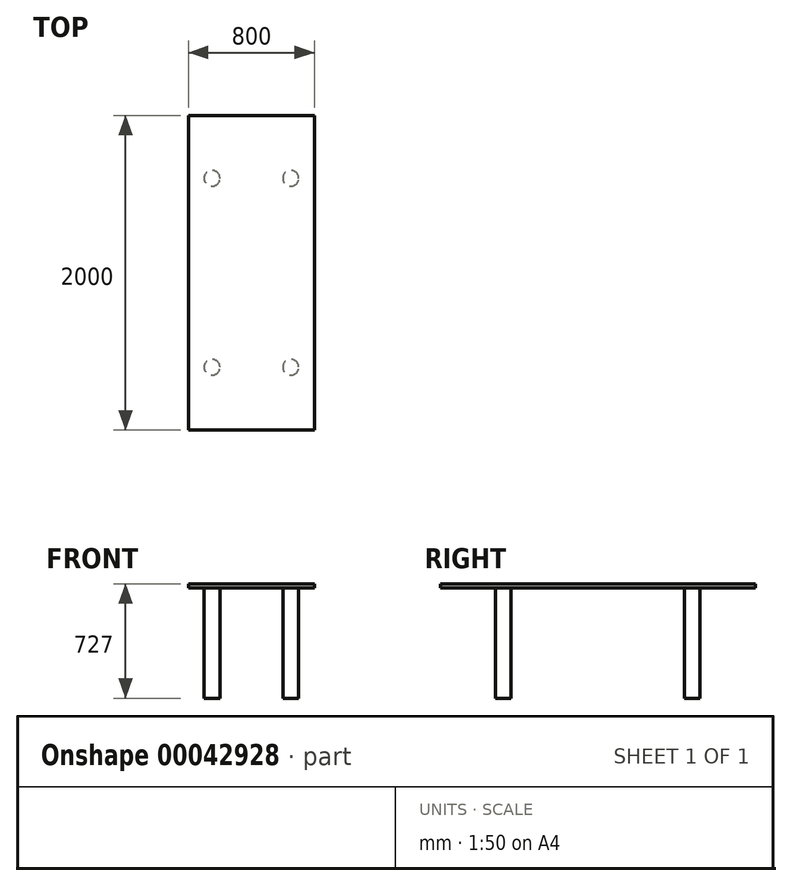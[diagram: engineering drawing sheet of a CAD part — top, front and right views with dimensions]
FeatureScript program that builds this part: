
annotation { "Feature Type Name" : "Feature", "Feature Type Description" : "" }
export const myFeature = defineFeature(function(context is Context, id is Id, definition is map)
    precondition{}
    {
        {
            var Q0;
            Q0=qCreatedBy(makeId("Front.planeOp"),FACE);
            var sketch = newSketch(context, id + "F0", { "sketchPlane" : qUnion([Q0])});
            skLineSegment(sketch, "E0.rect.bottom", {"start": v(400, 700) * mm, "end": v(-400, 700) * mm});
            skLineSegment(sketch, "E0.rect.top", {"start": v(400, 727) * mm, "end": v(-400, 727) * mm});
            skLineSegment(sketch, "E0.rect.left", {"start": v(400, 700) * mm, "end": v(400, 727) * mm});
            skLineSegment(sketch, "E0.rect.right", {"start": v(-400, 700) * mm, "end": v(-400, 727) * mm});
            skPoint(sketch, "E0.rect.middle", {"position": v(0, 713.5) * mm});
            skSolve(sketch);
        }
        {
            var Q0;
            Q0=makeQuery(id+"F0.imprint","IMPRINT",FACE,{"disambiguationData":[TD([[makeQuery(id+"F0.imprint","IMPRINT",EDGE,{"derivedFrom":sQuery(id+"F0.wireOp",EDGE,"E0.rect.bottom")}),-1.0]])]});
            extrude(context, id + "F1", {"entities" : qUnion([Q0]), "depth" : 2000 * mm});
        }
        {
            var Q0;
            Q0=makeQuery(id+"F1.opExtrude","SWEPT_FACE",FACE,{"disambiguationData":[OSD([sQuery(id+"F0.wireOp",EDGE,"E0.rect.bottom")])]});
            var sketch = newSketch(context, id + "F2", { "sketchPlane" : qUnion([Q0])});
            skCircle(sketch, "E1", {"center": v(-250, 400) * mm, "radius": 50.34 * mm});
            skCircle(sketch, "E2", {"center": v(-250, 1600) * mm, "radius": 50.34 * mm});
            skLineSegment(sketch, "E3", {"start": v(0, 0) * mm, "end": v(0, 2000) * mm, "construction": true});
            skCircle(sketch, "E4.MirrorC", {"center": v(250, 1600) * mm, "radius": 50.34 * mm});
            skCircle(sketch, "E5.MirrorC", {"center": v(250, 400) * mm, "radius": 50.34 * mm});
            skSolve(sketch);
        }
        {
            var Q0;
            Q0 = qSketchRegion(id + "F2", true);
            extrude(context, id + "F3", {"entities" : qUnion([Q0]), "operationType" : NewBodyOperationType.ADD, "depth" : 700 * mm});
        }
    });
